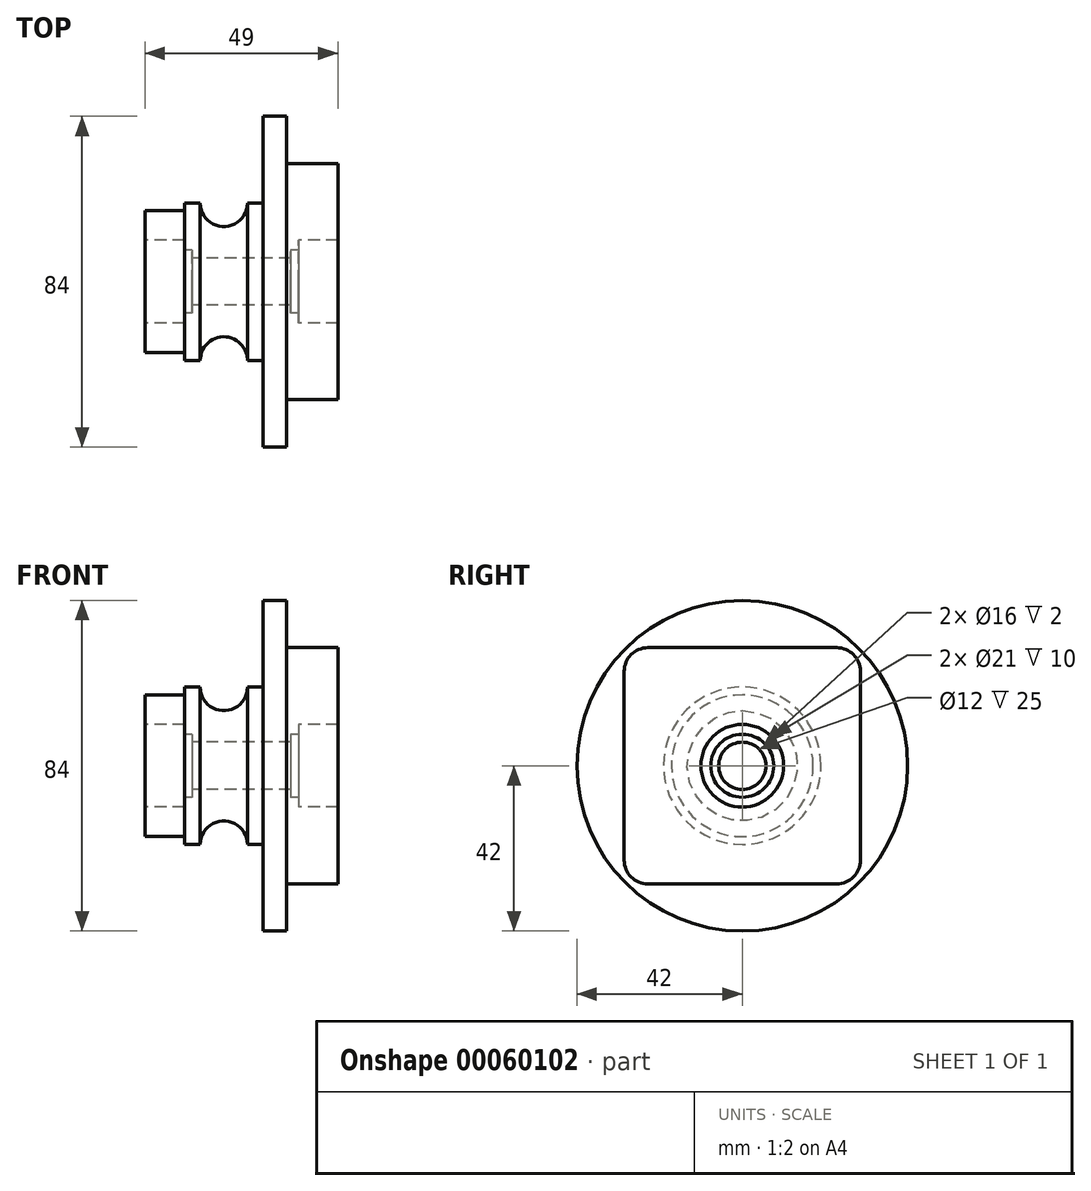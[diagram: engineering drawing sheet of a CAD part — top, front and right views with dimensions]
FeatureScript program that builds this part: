
annotation { "Feature Type Name" : "Feature", "Feature Type Description" : "" }
export const myFeature = defineFeature(function(context is Context, id is Id, definition is map)
    precondition{}
    {
        {
            var Q0;
            Q0=qCreatedBy(makeId("Front.planeOp"),FACE);
            var sketch = newSketch(context, id + "F0", { "sketchPlane" : qUnion([Q0])});
            skLineSegment(sketch, "E0", {"start": v(0, 0) * mm, "end": v(87.3, 0) * mm, "construction": true});
            skSolve(sketch);
        }
        {
            var Q0;
            Q0=qCreatedBy(makeId("Front.planeOp"),FACE);
            var sketch = newSketch(context, id + "F1", { "sketchPlane" : qUnion([Q0])});
            skLineSegment(sketch, "E1", {"start": v(0, 6) * mm, "end": v(-18, 6) * mm});
            skLineSegment(sketch, "E2", {"start": v(-20, 8) * mm, "end": v(-20, 10.5) * mm});
            skLineSegment(sketch, "E3", {"start": v(-20, 10.5) * mm, "end": v(-30, 10.5) * mm});
            skLineSegment(sketch, "E4", {"start": v(-30, 10.5) * mm, "end": v(-30, 18) * mm});
            skLineSegment(sketch, "E5", {"start": v(-30, 18) * mm, "end": v(-20, 18) * mm});
            skLineSegment(sketch, "E6", {"start": v(-20, 18) * mm, "end": v(-20, 20) * mm});
            skLineSegment(sketch, "E7", {"start": v(-20, 20) * mm, "end": v(-16, 20) * mm});
            skLineSegment(sketch, "E8", {"start": v(-4, 20) * mm, "end": v(0, 20) * mm});
            skLineSegment(sketch, "E9", {"start": v(0, 20) * mm, "end": v(0, 42) * mm});
            skLineSegment(sketch, "E10", {"start": v(0, 42) * mm, "end": v(6, 42) * mm});
            skLineSegment(sketch, "E11", {"start": v(6, 44) * mm, "end": v(6, 42) * mm});
            skLineSegment(sketch, "E12", {"start": v(6, 44) * mm, "end": v(19, 44) * mm});
            skLineSegment(sketch, "E13", {"start": v(19, 44) * mm, "end": v(19, 10.5) * mm});
            skLineSegment(sketch, "E14", {"start": v(19, 10.5) * mm, "end": v(9, 10.5) * mm});
            skLineSegment(sketch, "E15", {"start": v(9, 10.5) * mm, "end": v(9, 8) * mm});
            skLineSegment(sketch, "E16", {"start": v(7, 6) * mm, "end": v(0, 6) * mm});
            skArc(sketch, "E17", {"start": v(-4, 20) * mm, "mid": v(-10, 14) * mm, "end": v(-16, 20) * mm});
            skLineSegment(sketch, "E18.top", {"start": v(-20, 8) * mm, "end": v(-18, 8) * mm});
            skLineSegment(sketch, "E18.right", {"start": v(-18, 6) * mm, "end": v(-18, 8) * mm});
            skLineSegment(sketch, "E19.top", {"start": v(9, 8) * mm, "end": v(7, 8) * mm});
            skLineSegment(sketch, "E19.right", {"start": v(7, 6) * mm, "end": v(7, 8) * mm});
            skSolve(sketch);
        }
        {
            var Q0;
            Q0=makeQuery(id+"F1.imprint","IMPRINT",FACE,{"disambiguationData":[TD([[makeQuery(id+"F1.imprint","IMPRINT",EDGE,{"derivedFrom":sQuery(id+"F1.wireOp",EDGE,"E1")}),-1.0]])]});
            var Q1;
            Q1=sQuery(id+"F0.wireOp",EDGE,"E0");
            revolve(context, id + "F2", {"entities" : qUnion([Q0]), "axis" : qUnion([Q1]), "revolveType" : RevolveType.FULL});
        }
        {
            var Q0;
            Q0=makeQuery(id+"F2.opRevolve","SWEPT_FACE",FACE,{"disambiguationData":[OSD([sQuery(id+"F1.wireOp",EDGE,"E13")])]});
            var sketch = newSketch(context, id + "F3", { "sketchPlane" : qUnion([Q0])});
            skLineSegment(sketch, "E20.rect.bottom", {"start": v(30, 30) * mm, "end": v(-30, 30) * mm});
            skLineSegment(sketch, "E20.rect.top", {"start": v(30, -30) * mm, "end": v(-30, -30) * mm});
            skLineSegment(sketch, "E20.rect.left", {"start": v(30, 30) * mm, "end": v(30, -30) * mm});
            skLineSegment(sketch, "E20.rect.right", {"start": v(-30, 30) * mm, "end": v(-30, -30) * mm});
            skPoint(sketch, "E20.rect.middle", {"position": v(0, 0) * mm});
            skSolve(sketch);
        }
        {
            var Q0;
            Q0=makeQuery(id+"F3.imprint","IMPRINT",FACE,{"disambiguationData":[TD([[makeQuery(id+"F3.imprint","IMPRINT",EDGE,{"derivedFrom":sQuery(id+"F3.wireOp",EDGE,"E20.rect.bottom")}),-1.0]])]});
            var Q1;
            Q1=makeQuery(id+"F2.opRevolve","SWEPT_FACE",FACE,{"disambiguationData":[OSD([sQuery(id+"F1.wireOp",EDGE,"E11")])]});
            extrude(context, id + "F4", {"entities" : qUnion([Q0]), "operationType" : NewBodyOperationType.REMOVE, "endBound" : BoundingType.UP_TO_SURFACE, "oppositeDirection" : true, "endBoundEntityFace" : qUnion([Q1]), "depth" : 25 * mm});
        }
        {
            var Q0;
            Q0=makeQuery(id+"F4.boolean.opBoolean","COPY",EDGE,{"derivedFrom":makeQuery(id+"F4.opExtrude","SWEPT_EDGE",EDGE,{"disambiguationData":[OSD([sQuery(id+"F3.wireOp",EDGE,"E20.rect.top"),sQuery(id+"F3.wireOp",EDGE,"E20.rect.right")])]})});
            var Q1;
            Q1=makeQuery(id+"F4.boolean.opBoolean","COPY",EDGE,{"derivedFrom":makeQuery(id+"F4.opExtrude","SWEPT_EDGE",EDGE,{"disambiguationData":[OSD([sQuery(id+"F3.wireOp",EDGE,"E20.rect.top"),sQuery(id+"F3.wireOp",EDGE,"E20.rect.left")])]})});
            var Q2;
            Q2=makeQuery(id+"F4.boolean.opBoolean","COPY",EDGE,{"derivedFrom":makeQuery(id+"F4.opExtrude","SWEPT_EDGE",EDGE,{"disambiguationData":[OSD([sQuery(id+"F3.wireOp",EDGE,"E20.rect.bottom"),sQuery(id+"F3.wireOp",EDGE,"E20.rect.right")])]})});
            var Q3;
            Q3=makeQuery(id+"F4.boolean.opBoolean","COPY",EDGE,{"derivedFrom":makeQuery(id+"F4.opExtrude","SWEPT_EDGE",EDGE,{"disambiguationData":[OSD([sQuery(id+"F3.wireOp",EDGE,"E20.rect.bottom"),sQuery(id+"F3.wireOp",EDGE,"E20.rect.left")])]})});
            fillet(context, id + "F5", {"entities" : qUnion([Q0, Q1, Q2, Q3]), "radius" : 6 * mm, "tangentPropagation" : true, "allowEdgeOverflow" : false});
        }
    });
